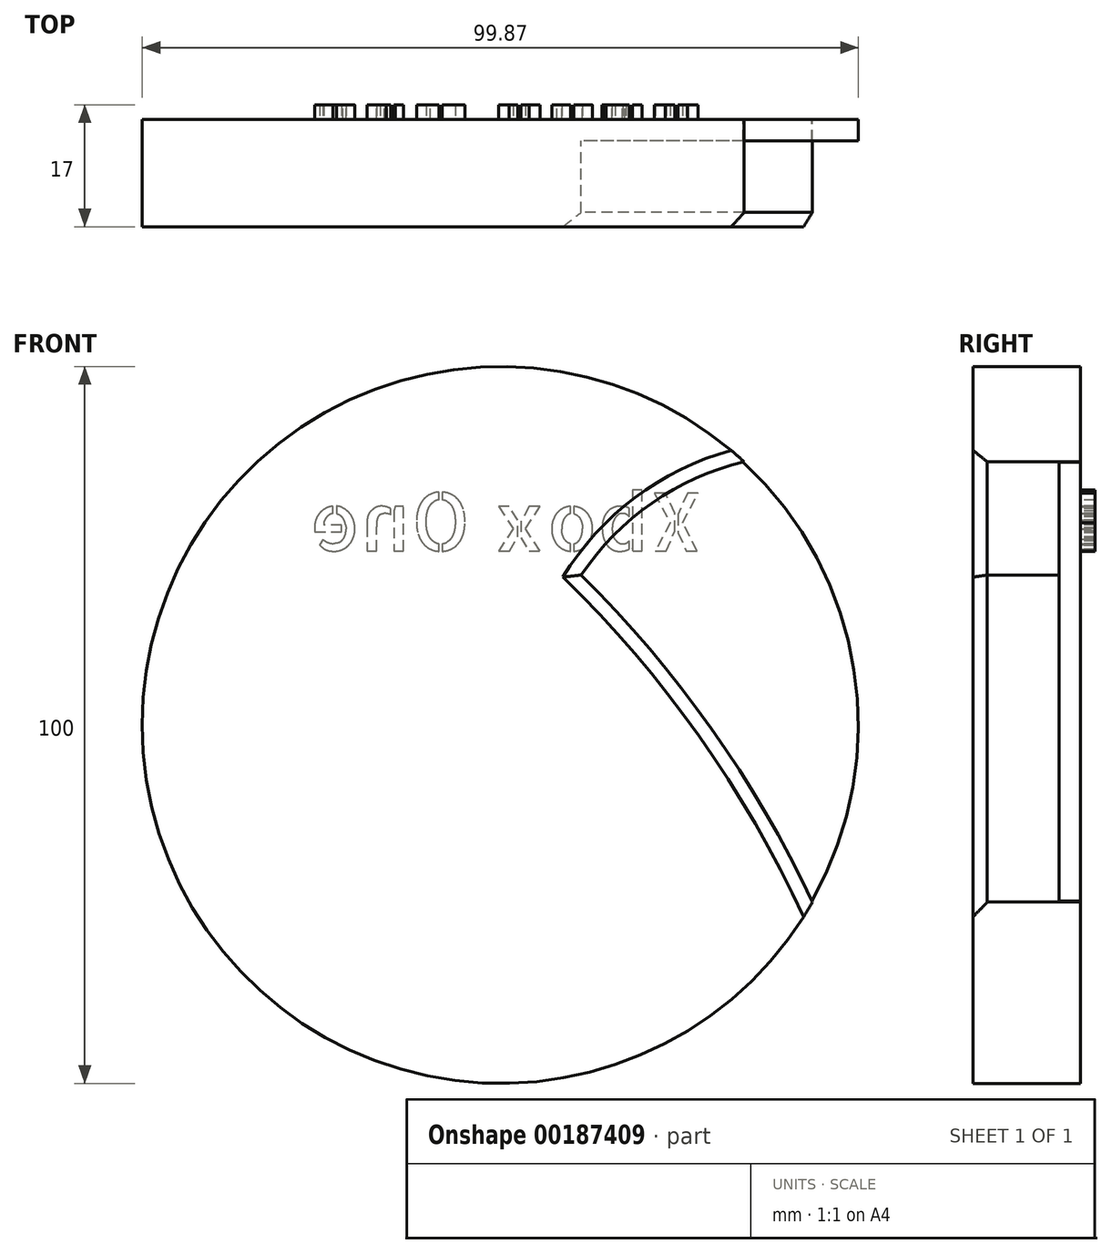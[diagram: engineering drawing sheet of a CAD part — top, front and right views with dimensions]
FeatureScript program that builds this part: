
annotation { "Feature Type Name" : "Feature", "Feature Type Description" : "" }
export const myFeature = defineFeature(function(context is Context, id is Id, definition is map)
    precondition{}
    {
        {
            var Q0;
            Q0=qCreatedBy(makeId("Front.planeOp"),FACE);
            var sketch = newSketch(context, id + "F0", { "sketchPlane" : qUnion([Q0])});
            skCircle(sketch, "E0", {"center": v(0, 0) * mm, "radius": 50 * mm});
            skArc(sketch, "E1", {"start": v(0, 30.74) * mm, "mid": v(-12.6, 41.02) * mm, "end": v(-28.85, 40.84) * mm});
            skArc(sketch, "E2.MirrorCS", {"start": v(0, 30.74) * mm, "mid": v(12.6, 41.02) * mm, "end": v(28.85, 40.84) * mm});
            skArc(sketch, "E3", {"start": v(-11.23, 20.92) * mm, "mid": v(-21.1, 30.97) * mm, "end": v(-33.96, 36.7) * mm});
            skArc(sketch, "E4.MirrorCS", {"start": v(11.23, 20.92) * mm, "mid": v(21.1, 30.97) * mm, "end": v(33.96, 36.7) * mm});
            skPoint(sketch, "E5.end.orphan", {"position": v(-46.88, -17.38) * mm});
            skPoint(sketch, "E6.end.orphan", {"position": v(-43.47, -24.7) * mm});
            skPoint(sketch, "E6.start.orphan", {"position": v(0, 6.6) * mm});
            skPoint(sketch, "E7.MirrorCS.end.orphan", {"position": v(43.47, -24.7) * mm});
            skPoint(sketch, "E8.MirrorCS.end.orphan", {"position": v(46.88, -17.38) * mm});
            skPoint(sketch, "E8.MirrorCS.start.orphan", {"position": v(11.23, 20.92) * mm});
            skArc(sketch, "E9", {"start": v(-11.23, 20.92) * mm, "mid": v(-29.35, -0.48) * mm, "end": v(-43.47, -24.7) * mm});
            skArc(sketch, "E10", {"start": v(0, 6.6) * mm, "mid": v(-22.05, -9.57) * mm, "end": v(-39.55, -30.59) * mm});
            skArc(sketch, "E11.MirrorCS", {"start": v(0, 6.6) * mm, "mid": v(22.05, -9.57) * mm, "end": v(39.55, -30.59) * mm});
            skArc(sketch, "E12.MirrorCS", {"start": v(11.23, 20.92) * mm, "mid": v(29.35, -0.48) * mm, "end": v(43.47, -24.7) * mm});
            skSolve(sketch);
        }
        {
            var Q0;
            {var subQ0=sQuery(id+"F0.wireOp",EDGE,"E3");Q0=makeQuery(id+"F0.imprint","IMPRINT",FACE,{"disambiguationData":[TD([[makeQuery(id+"F0.imprint","IMPRINT",EDGE,{"derivedFrom":subQ0}),1.0]])]});}
            var Q1;
            {var subQ0=sQuery(id+"F0.wireOp",EDGE,"E1");Q1=makeQuery(id+"F0.imprint","IMPRINT",FACE,{"disambiguationData":[TD([[makeQuery(id+"F0.imprint","IMPRINT",EDGE,{"derivedFrom":subQ0}),-1.0]])]});}
            var Q2;
            {var subQ0=sQuery(id+"F0.wireOp",EDGE,"E4.MirrorCS");Q2=makeQuery(id+"F0.imprint","IMPRINT",FACE,{"disambiguationData":[TD([[makeQuery(id+"F0.imprint","IMPRINT",EDGE,{"derivedFrom":subQ0}),-1.0]])]});}
            var Q3;
            {var subQ0=sQuery(id+"F0.wireOp",EDGE,"E10");Q3=makeQuery(id+"F0.imprint","IMPRINT",FACE,{"disambiguationData":[TD([[makeQuery(id+"F0.imprint","IMPRINT",EDGE,{"derivedFrom":subQ0}),1.0]])]});}
            extrude(context, id + "F1", {"entities" : qUnion([Q0, Q1, Q2, Q3]), "depth" : 15 * mm});
        }
        {
            var Q0;
            Q0=qCreatedBy(makeId("Front.planeOp"),FACE);
            var sketch = newSketch(context, id + "F2", { "sketchPlane" : qUnion([Q0])});
            skCircle(sketch, "E13", {"center": v(0, 0) * mm, "radius": 49.87 * mm});
            skSolve(sketch);
        }
        {
            var Q0;
            Q0=makeQuery(id+"F2.imprint","IMPRINT",FACE,{"disambiguationData":[TD([[makeQuery(id+"F2.imprint","IMPRINT",EDGE,{"derivedFrom":sQuery(id+"F2.wireOp",EDGE,"E13")}),1.0]])]});
            extrude(context, id + "F3", {"entities" : qUnion([Q0]), "depth" : 3 * mm});
        }
        {
            var Q0;
            Q0=makeQuery(id+"F3.opExtrude","SWEPT_BODY",BODY,{"disambiguationData":[OSD([sQuery(id+"F2.wireOp",EDGE,"E13")])]});
            var Q1;
            Q1=makeQuery(id+"F1.opExtrude","SWEPT_BODY",BODY,{"disambiguationData":[OSD([sQuery(id+"F0.wireOp",EDGE,"E0"),sQuery(id+"F0.wireOp",EDGE,"E4.MirrorCS"),sQuery(id+"F0.wireOp",EDGE,"E12.MirrorCS")])]});
            var Q2;
            Q2=makeQuery(id+"F1.opExtrude","SWEPT_BODY",BODY,{"disambiguationData":[OSD([sQuery(id+"F0.wireOp",EDGE,"E0"),sQuery(id+"F0.wireOp",EDGE,"E10"),sQuery(id+"F0.wireOp",EDGE,"E11.MirrorCS")])]});
            var Q3;
            Q3=makeQuery(id+"F1.opExtrude","SWEPT_BODY",BODY,{"disambiguationData":[OSD([sQuery(id+"F0.wireOp",EDGE,"E0"),sQuery(id+"F0.wireOp",EDGE,"E3"),sQuery(id+"F0.wireOp",EDGE,"E9")])]});
            var Q4;
            Q4=makeQuery(id+"F1.opExtrude","SWEPT_BODY",BODY,{"disambiguationData":[OSD([sQuery(id+"F0.wireOp",EDGE,"E0"),sQuery(id+"F0.wireOp",EDGE,"E1"),sQuery(id+"F0.wireOp",EDGE,"E2.MirrorCS")])]});
            booleanBodies(context, id + "F4", {"operationType" : BooleanOperationType.UNION, "tools" : qUnion([Q0, Q1, Q2, Q3, Q4])});
        }
        {
            var Q0;
            Q0=makeQuery(id+"F1.opExtrude","CAP_EDGE",EDGE,{"disambiguationData":[OSD([sQuery(id+"F0.wireOp",EDGE,"E3")])],"isStart":false});
            var Q1;
            Q1=makeQuery(id+"F1.opExtrude","CAP_EDGE",EDGE,{"disambiguationData":[OSD([sQuery(id+"F0.wireOp",EDGE,"E9")])],"isStart":false});
            var Q2;
            Q2=makeQuery(id+"F1.opExtrude","CAP_EDGE",EDGE,{"disambiguationData":[OSD([sQuery(id+"F0.wireOp",EDGE,"E10")])],"isStart":false});
            var Q3;
            Q3=makeQuery(id+"F1.opExtrude","CAP_EDGE",EDGE,{"disambiguationData":[OSD([sQuery(id+"F0.wireOp",EDGE,"E11.MirrorCS")])],"isStart":false});
            var Q4;
            Q4=makeQuery(id+"F1.opExtrude","CAP_EDGE",EDGE,{"disambiguationData":[OSD([sQuery(id+"F0.wireOp",EDGE,"E12.MirrorCS")])],"isStart":false});
            var Q5;
            Q5=makeQuery(id+"F1.opExtrude","CAP_EDGE",EDGE,{"disambiguationData":[OSD([sQuery(id+"F0.wireOp",EDGE,"E4.MirrorCS")])],"isStart":false});
            var Q6;
            Q6=makeQuery(id+"F1.opExtrude","CAP_EDGE",EDGE,{"disambiguationData":[OSD([sQuery(id+"F0.wireOp",EDGE,"E2.MirrorCS")])],"isStart":false});
            var Q7;
            Q7=makeQuery(id+"F1.opExtrude","CAP_EDGE",EDGE,{"disambiguationData":[OSD([sQuery(id+"F0.wireOp",EDGE,"E1")])],"isStart":false});
            chamfer(context, id + "F5", {"entities" : qUnion([Q0, Q1, Q2, Q3, Q4, Q5, Q6, Q7]), "width" : 2 * mm, "tangentPropagation" : true});
        }
        {
            var Q0;
            {var subQ0=sQuery(id+"F0.wireOp",EDGE,"E0");Q0=makeQuery(id+"F4.opBoolean","MERGE",FACE,{"derivedFrom":[makeQuery(id+"F1.opExtrude","CAP_FACE",FACE,{"disambiguationData":[OSD([subQ0,sQuery(id+"F0.wireOp",EDGE,"E1"),sQuery(id+"F0.wireOp",EDGE,"E2.MirrorCS")])],"isStart":true}),makeQuery(id+"F1.opExtrude","CAP_FACE",FACE,{"disambiguationData":[OSD([subQ0,sQuery(id+"F0.wireOp",EDGE,"E3"),sQuery(id+"F0.wireOp",EDGE,"E9")])],"isStart":true}),makeQuery(id+"F1.opExtrude","CAP_FACE",FACE,{"disambiguationData":[OSD([subQ0,sQuery(id+"F0.wireOp",EDGE,"E10"),sQuery(id+"F0.wireOp",EDGE,"E11.MirrorCS")])],"isStart":true}),makeQuery(id+"F1.opExtrude","CAP_FACE",FACE,{"disambiguationData":[OSD([subQ0,sQuery(id+"F0.wireOp",EDGE,"E4.MirrorCS"),sQuery(id+"F0.wireOp",EDGE,"E12.MirrorCS")])],"isStart":true}),makeQuery(id+"F3.opExtrude","CAP_FACE",FACE,{"disambiguationData":[OSD([sQuery(id+"F2.wireOp",EDGE,"E13")])],"isStart":true})]});}
            var sketch = newSketch(context, id + "F6", { "sketchPlane" : qUnion([Q0])});
            skText(sketch, "E14", { "text": "Xbox One", "fontName": "AllertaStencil-Regular.ttf"});
            const initialGuessF6  = {"E14": [-0.02836, 0.02427, 1, 0, 0.0081]};
            skSetInitialGuess(sketch, initialGuessF6);
            skSolve(sketch);
        }
        {
            var Q0;
            Q0 = qSketchRegion(id + "F6", true);
            extrude(context, id + "F7", {"entities" : qUnion([Q0]), "operationType" : NewBodyOperationType.ADD, "depth" : 2 * mm});
        }
    });
